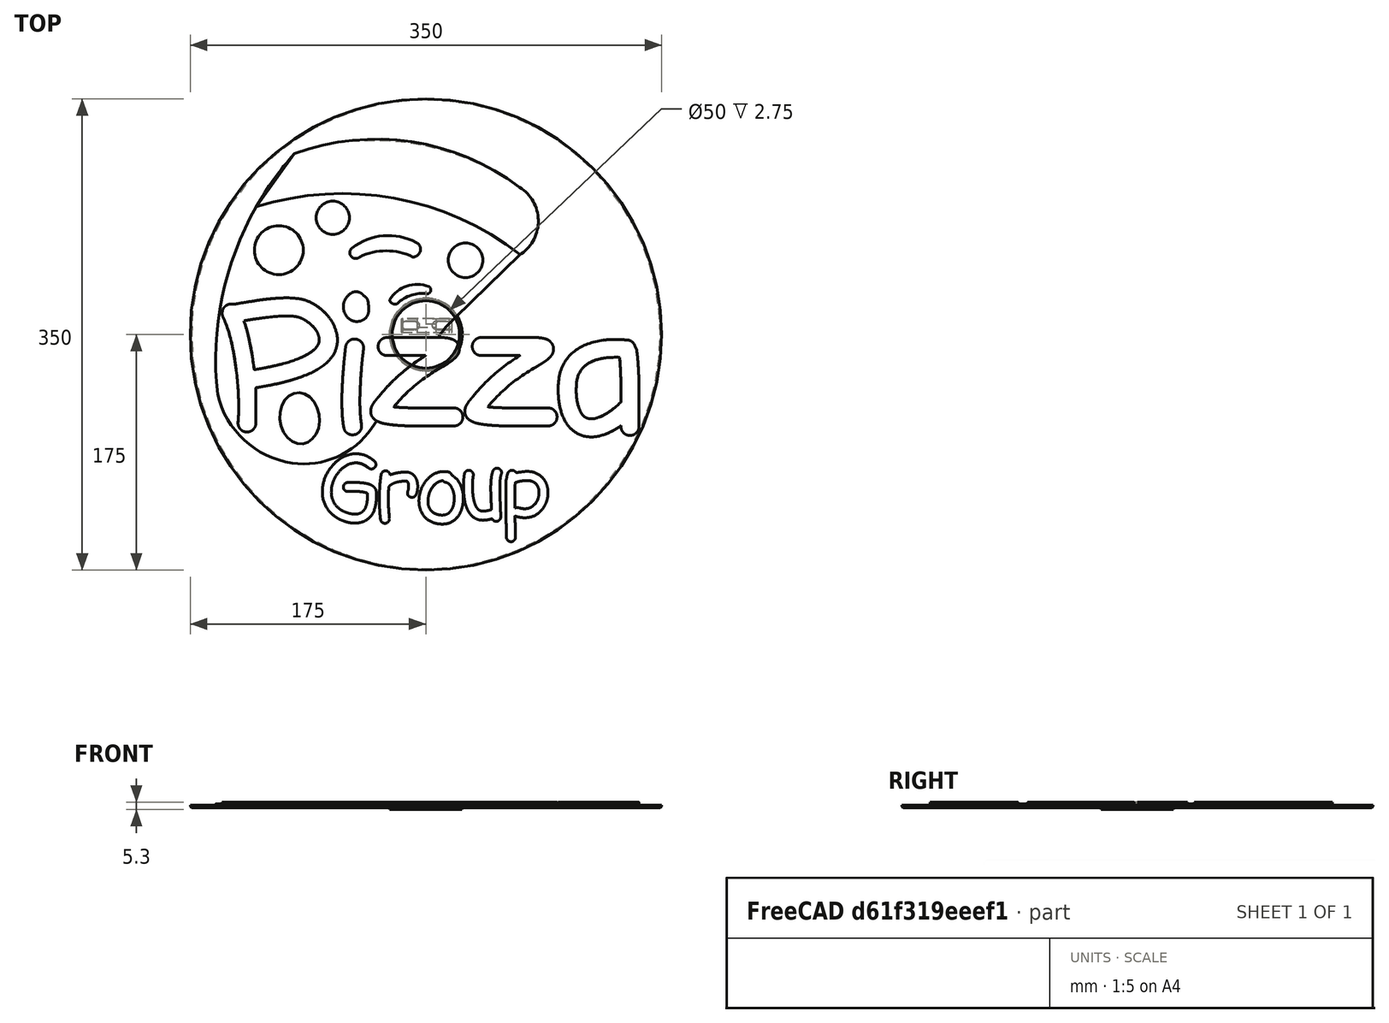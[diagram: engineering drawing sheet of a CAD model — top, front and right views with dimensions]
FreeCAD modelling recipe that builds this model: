
FCSTD DOCUMENT  (FreeCAD 1.2R20260217 (Git shallow))
Label: pizza
License: All rights reserved
LicenseURL: https://en.wikipedia.org/wiki/All_rights_reserved
objects: Sketcher::SketchObject×8, PartDesign::Pad×7, PartDesign::Pocket×3, App::Point×2, Part::Part2DObjectPython×2, Part::Feature×2, PartDesign::Fillet×2, PartDesign::Body×2, Image::ImagePlane×1, Mesh::Feature×1, Part::Refine×1, PartDesign::Chamfer×1, Measure::MeasureArea×1
note: 62 computed .brp shape members not serialized (recipe doc carries the construction recipe); baked Part::Feature solids carry a one-line shape summary decoded from their .brp

FEATURE [App::Point] Origin001
  Role = Origin
FEATURE [Image::ImagePlane] pizza
  XSize = 329.894
  YSize = 323.28
FEATURE [Sketcher::SketchObject] Sketch
  ArcFitTolerance = 1e-06
  AttachmentSupport = -> [Origin]
  ExternalTypes = [0]
  FullyConstrained = false
  MakeInternals = false
  MapMode = 5
  sketch-geometry (7):
    g0: ArcOfCircle CenterX=-38.528 CenterY=-41.7766 CenterZ=0 NormalX=0 NormalY=0 NormalZ=1 AngleXU=0 Radius=185.777 StartAngle=0.949344 EndAngle=1.89447
    g1: ArcOfCircle CenterX=53.94 CenterY=84.1856 CenterZ=0 NormalX=0 NormalY=0 NormalZ=1 AngleXU=0 Radius=29.5866 StartAngle=5.28648 EndAngle=7.29484
    g2: LineSegment StartX=70.0078 StartY=59.3422 StartZ=0 EndX=14.8481 EndY=5.69801 EndZ=0
    g3: LineSegment StartX=14.8481 StartY=5.69801 StartZ=0 EndX=-40.3047 EndY=-69.5254 EndZ=0
    g4: ArcOfCircle CenterX=-90.4866 CenterY=-35.4959 CenterZ=0 NormalX=0 NormalY=0 NormalZ=1 AngleXU=0 Radius=60.6319 StartAngle=4.56467 EndAngle=5.68729
    g5: ArcOfCircle CenterX=-89.5728 CenterY=-29.3547 CenterZ=0 NormalX=0 NormalY=0 NormalZ=1 AngleXU=0 Radius=66.8407 StartAngle=3.36899 EndAngle=4.56467
    g6: ArcOfCircle CenterX=74.4265 CenterY=-19.0735 CenterZ=0 NormalX=0 NormalY=0 NormalZ=1 AngleXU=0 Radius=230.517 StartAngle=2.41333 EndAngle=3.25178
  constraints (7):
    c: Coincident(g1,g0)
    c: Coincident(g2,g1)
    c: Coincident(g3,g2)
    c: Coincident(g4,g3)
    c: Coincident(g6,g5)
    c: Tangent(g5,g4) = -1.5708
    c: Coincident(g0,g6)
FEATURE [PartDesign::Pad] Pad
  Direction = (0,0,1)
  Length = 3
  Length2 = 10
  Profile = -> Sketch
  ReferenceAxis = -> Sketch [N_Axis]
  Refine = true
  SideType = 0
  Suppressed = false
  Type = 0
  Type2 = 0
FEATURE [Sketcher::SketchObject] Sketch002
  ArcFitTolerance = 1e-06
  AttachmentSupport = -> [Pad]
  ExternalTypes = [0]
  FullyConstrained = false
  MakeInternals = false
  MapMode = 5
  Placement = pos=(0,0,3) rot=(0,0,1;0rad)
  sketch-geometry (16):
    g0: Circle CenterX=-109.242 CenterY=62.5751 CenterZ=0 NormalX=0 NormalY=0 NormalZ=1 AngleXU=0 Radius=18.1491
    g1: Ellipse CenterX=-93.7692 CenterY=-62.3523 CenterZ=0 NormalX=0 NormalY=0 NormalZ=1 MajorRadius=19.0963 MinorRadius=14.7094 AngleXU=-1.45046
    g2: LineSegment [constr] StartX=-91.4767 StartY=-81.3105 StartZ=0 EndX=-96.0617 EndY=-43.3941 EndZ=0
    g3: LineSegment [constr] StartX=-79.1662 StartY=-60.5864 StartZ=0 EndX=-108.372 EndY=-64.1182 EndZ=0
    g4: GeomPoint [constr] X=-92.3072 Y=-74.4421 Z=0
    g5: GeomPoint [constr] X=-95.2312 Y=-50.2625 Z=0
    g6: Circle CenterX=-69.1275 CenterY=86.6438 CenterZ=0 NormalX=0 NormalY=0 NormalZ=1 AngleXU=0 Radius=12.309
    g7: Circle CenterX=29.4391 CenterY=55.1253 CenterZ=0 NormalX=0 NormalY=0 NormalZ=1 AngleXU=0 Radius=12.8434
    g8: ArcOfCircle CenterX=-27.7695 CenterY=29.0075 CenterZ=0 NormalX=0 NormalY=0 NormalZ=1 AngleXU=0 Radius=44.3733 StartAngle=1.08765 EndAngle=2.22723
    g9: ArcOfCircle CenterX=-29.4723 CenterY=17.4728 CenterZ=0 NormalX=0 NormalY=0 NormalZ=1 AngleXU=0 Radius=44.6242 StartAngle=1.11353 EndAngle=2.027
    g10: ArcOfCircle CenterX=-52.1082 CenterY=60.7448 CenterZ=0 NormalX=0 NormalY=0 NormalZ=1 AngleXU=0 Radius=4.37894 StartAngle=2.24749 EndAngle=5.45989
    g11: ArcOfCircle CenterX=-9.62401 CenterY=63.1885 CenterZ=0 NormalX=0 NormalY=0 NormalZ=1 AngleXU=0 Radius=5.678 StartAngle=4.68655 EndAngle=7.40414
    g12: ArcOfCircle CenterX=-6.32186 CenterY=12.5996 CenterZ=0 NormalX=0 NormalY=0 NormalZ=1 AngleXU=0 Radius=24.5414 StartAngle=1.21694 EndAngle=2.57253
    g13: ArcOfCircle CenterX=-2.72099 CenterY=4.19567 CenterZ=0 NormalX=0 NormalY=0 NormalZ=1 AngleXU=0 Radius=26.2805 StartAngle=1.42206 EndAngle=2.34974
    g14: ArcOfCircle CenterX=-23.0173 CenterY=26.4917 CenterZ=0 NormalX=0 NormalY=0 NormalZ=1 AngleXU=0 Radius=4.03406 StartAngle=3.30796 EndAngle=5.18423
    g15: ArcOfCircle CenterX=0.846789 CenterY=33.0576 CenterZ=0 NormalX=0 NormalY=0 NormalZ=1 AngleXU=0 Radius=2.89002 StartAngle=4.82563 EndAngle=7.37365
  constraints (9):
    c: InternalAlignment(g2-g5 -> g1) x4
    c: Coincident(g10,g8)
    c: Coincident(g10,g9)
    c: Coincident(g11,g8)
    c: Coincident(g11,g9)
    c: Coincident(g14,g12)
    c: Coincident(g14,g13)
    c: Coincident(g15,g13)
    c: Coincident(g15,g12)
FEATURE [Sketcher::SketchObject] Sketch001
  ArcFitTolerance = 1e-06
  AttachmentSupport = -> [Pad]
  ExternalGeometry = -> [Pad]
  ExternalTypes = [0,0,0]
  FullyConstrained = false
  MakeInternals = false
  MapMode = 5
  Placement = pos=(0,0,3) rot=(0,0,1;0rad)
  sketch-geometry (3):
    g0: ArcOfCircle CenterX=-61.9197 CenterY=-110.411 CenterZ=0 NormalX=0 NormalY=0 NormalZ=1 AngleXU=0 Radius=214.99 StartAngle=0.91013 EndAngle=1.87344
    g1: LineSegment StartX=-125.996 StartY=94.8092 StartZ=0 EndX=-97.6152 EndY=134.354 EndZ=0
    g2: ArcOfCircle CenterX=-37.0878 CenterY=-32.1751 CenterZ=0 NormalX=0 NormalY=0 NormalZ=1 AngleXU=0 Radius=177.187 StartAngle=0.9244 EndAngle=1.91942
  constraints (4):
    c: Coincident(g0,g-3)
    c: Coincident(g1,g0)
    c: Coincident(g2,g1)
    c: Coincident(g2,g-3)
FEATURE [PartDesign::Pad] Pad001
  BaseFeature = -> Pad
  Direction = (0,0,1)
  Length = 1
  Length2 = 10
  Profile = -> Sketch001
  ReferenceAxis = -> Sketch001 [N_Axis]
  Refine = true
  SideType = 0
  Suppressed = false
  Type = 0
  Type2 = 0
FEATURE [PartDesign::Pad] Pad002
  BaseFeature = -> Pad001
  Direction = (0,0,1)
  Length = 1
  Length2 = 10
  Profile = -> Sketch002
  ReferenceAxis = -> Sketch002 [N_Axis]
  Refine = true
  SideType = 0
  Suppressed = false
  Type = 0
  Type2 = 0
FEATURE [Sketcher::SketchObject] Sketch003
  ArcFitTolerance = 1e-06
  AttachmentSupport = -> [Origin]
  ExternalTypes = [0]
  FullyConstrained = true
  MakeInternals = false
  MapMode = 5
  sketch-geometry (1):
    g0: Circle CenterX=0 CenterY=0 CenterZ=0 NormalX=0 NormalY=0 NormalZ=1 AngleXU=0 Radius=175
  constraints (2):
    c: Diameter(g0) = 350
    c: Coincident(g0,g-1)
FEATURE [PartDesign::Pad] Pad003
  BaseFeature = -> Pad002
  Direction = (0,0,1)
  Length = 2
  Length2 = 10
  Profile = -> Sketch003
  ReferenceAxis = -> Sketch003 [N_Axis]
  Refine = true
  SideType = 0
  Suppressed = false
  Type = 0
  Type2 = 0
FEATURE [Part::Part2DObjectPython] ShapeString  # Draft 2D object (typed FeaturePython)
  FontFile = <userpath>/Downloads/qd-better-comic-sans-font/Qdbettercomicsans-jEEeG.ttf
  Fuse = false
  Justification = 6
  JustificationReference = 0
  KeepLeftMargin = false
  MakeFace = true
  ObliqueAngle = 0
  Placement = pos=(-151.304,-72.778,0) rot=(0,0,1;0rad)
  ScaleToSize = true
  Size = 100
  String = Pizza
  Tracking = 0
FEATURE [Part::Part2DObjectPython] ShapeString001  # Draft 2D object (typed FeaturePython)
  FontFile = <userpath>/Downloads/qd-better-comic-sans-font/Qdbettercomicsans-jEEeG.ttf
  Fuse = false
  Justification = 6
  JustificationReference = 0
  KeepLeftMargin = false
  MakeFace = true
  ObliqueAngle = 0
  Placement = pos=(-76.8849,-137.984,0) rot=(0,0,1;0rad)
  ScaleToSize = true
  Size = 50
  String = Group
  Tracking = 0
FEATURE [PartDesign::Pad] Pad004
  BaseFeature = -> Pad003
  Direction = (0,0,1)
  Length = 4
  Length2 = 10
  Profile = -> ShapeString
  ReferenceAxis = -> ShapeString [N_Axis]
  Refine = true
  SideType = 0
  Suppressed = false
  Type = 0
  Type2 = 0
FEATURE [PartDesign::Pad] Pad005
  BaseFeature = -> Pad004
  Direction = (0,0,1)
  Length = 4
  Length2 = 10
  Profile = -> ShapeString001
  ReferenceAxis = -> ShapeString001 [N_Axis]
  Refine = true
  SideType = 0
  Suppressed = false
  Type = 0
  Type2 = 0
FEATURE [App::Point] Origin003
  Role = Origin
FEATURE [Sketcher::SketchObject] Sketch004
  ArcFitTolerance = 1e-06
  AttachmentSupport = -> [Origin002]
  ExternalTypes = [0]
  FullyConstrained = true
  MakeInternals = false
  MapMode = 5
  sketch-geometry (1):
    g0: Circle CenterX=0 CenterY=0 CenterZ=0 NormalX=0 NormalY=0 NormalZ=1 AngleXU=0 Radius=27
  constraints (2):
    c: Coincident(g0,g-1)
    c: Diameter(g0) = 54
FEATURE [PartDesign::Pad] Pad006
  Direction = (0,0,1)
  Length = 4
  Length2 = 10
  Profile = -> Sketch004
  ReferenceAxis = -> Sketch004 [N_Axis]
  Refine = true
  SideType = 0
  Suppressed = false
  Type = 0
  Type2 = 0
FEATURE [Sketcher::SketchObject] Sketch005
  ArcFitTolerance = 1e-06
  AttachmentSupport = -> [Pad006]
  ExternalTypes = [0]
  FullyConstrained = true
  MakeInternals = false
  MapMode = 5
  Placement = pos=(0,0,4) rot=(0,0,1;0rad)
  sketch-geometry (1):
    g0: Circle CenterX=0 CenterY=0 CenterZ=0 NormalX=0 NormalY=0 NormalZ=1 AngleXU=0 Radius=25
  constraints (2):
    c: Coincident(g0,g-1)
    c: Diameter(g0) = 50
FEATURE [PartDesign::Pocket] Pocket
  BaseFeature = -> Pad006
  Direction = (0,0,-1)
  Length = 2.75
  Length2 = 5
  Profile = -> Sketch005
  ReferenceAxis = -> Sketch005 [N_Axis]
  Refine = true
  SideType = 0
  Suppressed = false
  Type = 0
  Type2 = 0
FEATURE [Sketcher::SketchObject] Sketch006
  ArcFitTolerance = 1e-06
  AttachmentSupport = -> [Pocket]
  ExternalTypes = [0]
  FullyConstrained = false
  MakeInternals = false
  MapMode = 5
  Placement = pos=(0,0,1.25) rot=(0,0,1;0rad)
  sketch-geometry (22):
    g0: LineSegment StartX=-18.3419 StartY=7.5 StartZ=0 EndX=-18.3419 EndY=5.50529 EndZ=0
    g1: LineSegment StartX=-16.3419 StartY=3.50529 StartZ=0 EndX=-8.19187 EndY=3.50529 EndZ=0
    g2: LineSegment StartX=-6.19187 StartY=5.50529 StartZ=0 EndX=-6.19187 EndY=7.5 EndZ=0
    g3: LineSegment StartX=-8.19187 StartY=9.5 StartZ=0 EndX=-16.3419 EndY=9.5 EndZ=0
    g4: LineSegment StartX=7.30813 StartY=7.5 StartZ=0 EndX=7.30813 EndY=5.5 EndZ=0
    g5: LineSegment StartX=9.30813 StartY=3.5 StartZ=0 EndX=17.4581 EndY=3.5 EndZ=0
    g6: LineSegment StartX=19.4581 StartY=5.5 StartZ=0 EndX=19.4581 EndY=7.5 EndZ=0
    g7: LineSegment StartX=17.4581 StartY=9.5 StartZ=0 EndX=9.30813 EndY=9.5 EndZ=0
    g8: ArcOfCircle CenterX=-8.19187 CenterY=7.5 CenterZ=0 NormalX=0 NormalY=0 NormalZ=1 AngleXU=0 Radius=2 StartAngle=1.1e-15 EndAngle=1.5708
    g9: GeomPoint [constr] X=-6.19187 Y=9.5 Z=0
    g10: ArcOfCircle CenterX=-8.19187 CenterY=5.50529 CenterZ=0 NormalX=0 NormalY=0 NormalZ=1 AngleXU=0 Radius=2 StartAngle=4.71239 EndAngle=6.28319
    g11: ArcOfCircle CenterX=-16.3419 CenterY=5.50529 CenterZ=0 NormalX=0 NormalY=0 NormalZ=1 AngleXU=0 Radius=2 StartAngle=3.14159 EndAngle=4.71239
    g12: GeomPoint [constr] X=-18.3419 Y=3.50529 Z=0
    g13: ArcOfCircle CenterX=-16.3419 CenterY=7.5 CenterZ=0 NormalX=0 NormalY=0 NormalZ=1 AngleXU=0 Radius=2 StartAngle=1.5708 EndAngle=3.14159
    g14: GeomPoint [constr] X=-18.3419 Y=9.5 Z=0
    g15: ArcOfCircle CenterX=9.30813 CenterY=7.5 CenterZ=0 NormalX=0 NormalY=0 NormalZ=1 AngleXU=0 Radius=2 StartAngle=1.5708 EndAngle=3.14159
    g16: GeomPoint [constr] X=7.30813 Y=9.5 Z=0
    g17: ArcOfCircle CenterX=17.4581 CenterY=7.5 CenterZ=0 NormalX=0 NormalY=0 NormalZ=1 AngleXU=0 Radius=2 StartAngle=0 EndAngle=1.5708
    g18: GeomPoint [constr] X=19.4581 Y=9.5 Z=0
    g19: ArcOfCircle CenterX=17.4581 CenterY=5.5 CenterZ=0 NormalX=0 NormalY=0 NormalZ=1 AngleXU=0 Radius=2 StartAngle=4.71239 EndAngle=6.28319
    g20: GeomPoint [constr] X=19.4581 Y=3.5 Z=0
    g21: ArcOfCircle CenterX=9.30813 CenterY=5.5 CenterZ=0 NormalX=0 NormalY=0 NormalZ=1 AngleXU=0 Radius=2 StartAngle=3.14159 EndAngle=4.71239
  constraints (50):
    c: Vertical(g0)
    c: Vertical(g2)
    c: Horizontal(g1)
    c: Horizontal(g3)
    c: Vertical(g4)
    c: Vertical(g6)
    c: Horizontal(g5)
    c: Horizontal(g7)
    c: Horizontal(g16,g9)
    c: DistanceY(g20,g18) = 6
    c: DistanceY(g-1,g20) = 3.5
    c: PointOnObject(g9,g3)
    c: PointOnObject(g9,g2)
    c: Tangent(g3,g8) = -1.5708
    c: Tangent(g2,g8) = -1.5708
    c: Tangent(g2,g10) = -1.5708
    c: Tangent(g1,g10) = -1.5708
    c: PointOnObject(g12,g0)
    c: PointOnObject(g12,g1)
    c: Tangent(g0,g11) = -1.5708
    c: Tangent(g1,g11) = -1.5708
    c: PointOnObject(g14,g0)
    c: PointOnObject(g14,g3)
    c: Tangent(g0,g13) = -1.5708
    c: Tangent(g3,g13) = -1.5708
    c: PointOnObject(g16,g7)
    c: PointOnObject(g16,g4)
    c: Tangent(g7,g15) = -1.5708
    c: Tangent(g4,g15) = -1.5708
    c: PointOnObject(g18,g6)
    c: PointOnObject(g18,g7)
    c: Tangent(g6,g17) = -1.5708
    c: Tangent(g7,g17) = -1.5708
    c: PointOnObject(g20,g5)
    c: PointOnObject(g20,g6)
    c: Tangent(g5,g19) = -1.5708
    c: Tangent(g6,g19) = -1.5708
    c: Tangent(g4,g21) = -1.5708
    c: Tangent(g5,g21) = -1.5708
    c: Equal(g10,g8)
    c: Equal(g8,g13)
    c: Equal(g13,g11)
    c: Equal(g11,g21)
    c: Equal(g21,g15)
    c: Equal(g15,g17)
    c: Equal(g17,g19)
    c: Radius(g8) = 2
    c: DistanceX(g2,g4) = 13.5
    c: DistanceX(g4,g6) = 12.15
    c: DistanceX(g0,g2) = 12.15
FEATURE [PartDesign::Pocket] Pocket001
  BaseFeature = -> Pocket
  Direction = (0,0,-1)
  Length = 5
  Length2 = 5
  Profile = -> Sketch006
  ReferenceAxis = -> Sketch006 [N_Axis]
  Refine = true
  SideType = 0
  Suppressed = false
  Type = 0
  Type2 = 0
FEATURE [Sketcher::SketchObject] Sketch007
  ArcFitTolerance = 1e-06
  AttachmentSupport = -> [Pocket001]
  ExternalGeometry = -> [Sketch006]
  ExternalTypes = [0,0,0,0,0,0]
  FullyConstrained = false
  MakeInternals = false
  MapMode = 5
  Placement = pos=(0,0,1.25) rot=(0,0,1;0rad)
  sketch-geometry (13):
    g0: LineSegment StartX=-18.3419 StartY=11.5 StartZ=0 EndX=-18.3419 EndY=1.5 EndZ=0
    g1: LineSegment StartX=-18.3419 StartY=1.5 StartZ=0 EndX=-6.19187 EndY=1.5 EndZ=0
    g2: LineSegment StartX=-6.19187 StartY=1.5 StartZ=0 EndX=-6.19187 EndY=5.50529 EndZ=0
    g3: LineSegment StartX=-6.19187 StartY=11.5 StartZ=0 EndX=-18.3419 EndY=11.5 EndZ=0
    g4: LineSegment StartX=7.30813 StartY=11.5 StartZ=0 EndX=7.30813 EndY=7.5 EndZ=0
    g5: LineSegment StartX=7.30813 StartY=1.5 StartZ=0 EndX=19.4581 EndY=1.5 EndZ=0
    g6: LineSegment StartX=19.4581 StartY=1.5 StartZ=0 EndX=19.4581 EndY=11.5 EndZ=0
    g7: LineSegment StartX=19.4581 StartY=11.5 StartZ=0 EndX=7.30813 EndY=11.5 EndZ=0
    g8: LineSegment StartX=-6.19187 StartY=5.50529 StartZ=0 EndX=-6.19187 EndY=5.5 EndZ=0
    g9: LineSegment StartX=-6.19187 StartY=5.5 StartZ=0 EndX=7.30813 EndY=5.5 EndZ=0
    g10: LineSegment StartX=7.30813 StartY=7.5 StartZ=0 EndX=-6.19187 EndY=7.5 EndZ=0
    g11: LineSegment StartX=-6.19187 StartY=7.5 StartZ=0 EndX=-6.19187 EndY=11.5 EndZ=0
    g12: LineSegment StartX=7.30813 StartY=5.5 StartZ=0 EndX=7.30813 EndY=1.5 EndZ=0
  constraints (32):
    c: Coincident(g0,g1)
    c: Coincident(g1,g2)
    c: Coincident(g11,g3)
    c: Coincident(g3,g0)
    c: Vertical(g0)
    c: Horizontal(g1)
    c: Horizontal(g3)
    c: Coincident(g12,g5)
    c: Coincident(g5,g6)
    c: Coincident(g6,g7)
    c: Coincident(g7,g4)
    c: Vertical(g6)
    c: Horizontal(g5)
    c: Horizontal(g7)
    c: PointOnObject(g-3,g6)
    c: PointOnObject(g-6,g0)
    c: DistanceY(g-7,g6) = 2
    c: DistanceY(g5,g-8) = 2
    c: Horizontal(g11,g4)
    c: Coincident(g8,g9)
    c: Horizontal(g9)
    c: Horizontal(g10)
    c: Coincident(g9,g-5)
    c: Vertical(g2)
    c: Vertical(g11)
    c: Coincident(g2,g-4)
    c: Vertical(g4)
    c: Vertical(g12)
    c: Coincident(g4,g10)
    c: Coincident(g12,g9)
    c: Vertical(g8)
    c: Coincident(g8,g2)
FEATURE [PartDesign::Pocket] Pocket002
  BaseFeature = -> Pocket001
  Direction = (0,0,-1)
  Length = 0.75
  Length2 = 5
  Profile = -> Sketch007
  ReferenceAxis = -> Sketch007 [N_Axis]
  Refine = true
  SideType = 0
  Suppressed = false
  Type = 0
  Type2 = 0
FEATURE [Part::Feature] OpenDnD_Pin_Back002_solid  label="OpenDnD_Pin_Back002 (Solid)"
  shape: bbox 53.8 x 53.8 x 3.5 mm, 1440 faces (baked)
FEATURE [Mesh::Feature] OpenDnD_Pin_Back
FEATURE [Part::Feature] OpenDnD_Pin_Back001
  shape: bbox 53.8 x 53.8 x 3.5 mm, 2596 faces, 0 solids (baked)
FEATURE [Part::Refine] OpenDnD_Pin_Back002
  Source = -> OpenDnD_Pin_Back001
FEATURE [PartDesign::Fillet] Fillet001
  Base = -> Pocket002 [Edge3]
  BaseFeature = -> Pocket002
  Radius = 1.99
  Refine = true
  SupportTransform = false
  Suppressed = false
  UseAllEdges = false
FEATURE [PartDesign::Body] Body001
  AllowCompound = true
  Group = -> [Sketch004,Pad006,Sketch005,Pocket,Sketch006,Pocket001,Sketch007,Pocket002,Fillet001]
  Origin = -> Origin002
  Tip = -> Fillet001
FEATURE [PartDesign::Fillet] Fillet
  Base = -> Pad005 [Edge831]
  BaseFeature = -> Pad005
  Radius = 0.99
  Refine = true
  SupportTransform = false
  Suppressed = false
  UseAllEdges = false
FEATURE [PartDesign::Chamfer] Chamfer
  Angle = 45
  Base = -> Fillet [Edge343]
  BaseFeature = -> Fillet
  ChamferType = 0
  FlipDirection = false
  Refine = true
  Size = 1
  Size2 = 1
  SupportTransform = false
  Suppressed = false
  UseAllEdges = false
FEATURE [PartDesign::Body] Body
  AllowCompound = true
  Group = -> [Sketch,Pad,Sketch001,Pad001,Sketch002,Pad002,Sketch003,Pad003,ShapeString,ShapeString001,Pad004,Pad005,Fillet,Chamfer]
  Origin = -> Origin
  Tip = -> Chamfer
FEATURE [Measure::MeasureArea] Area  label="Area: 1966.93 cm^2"
  Area = 196693
  Elements = -> [Body]
